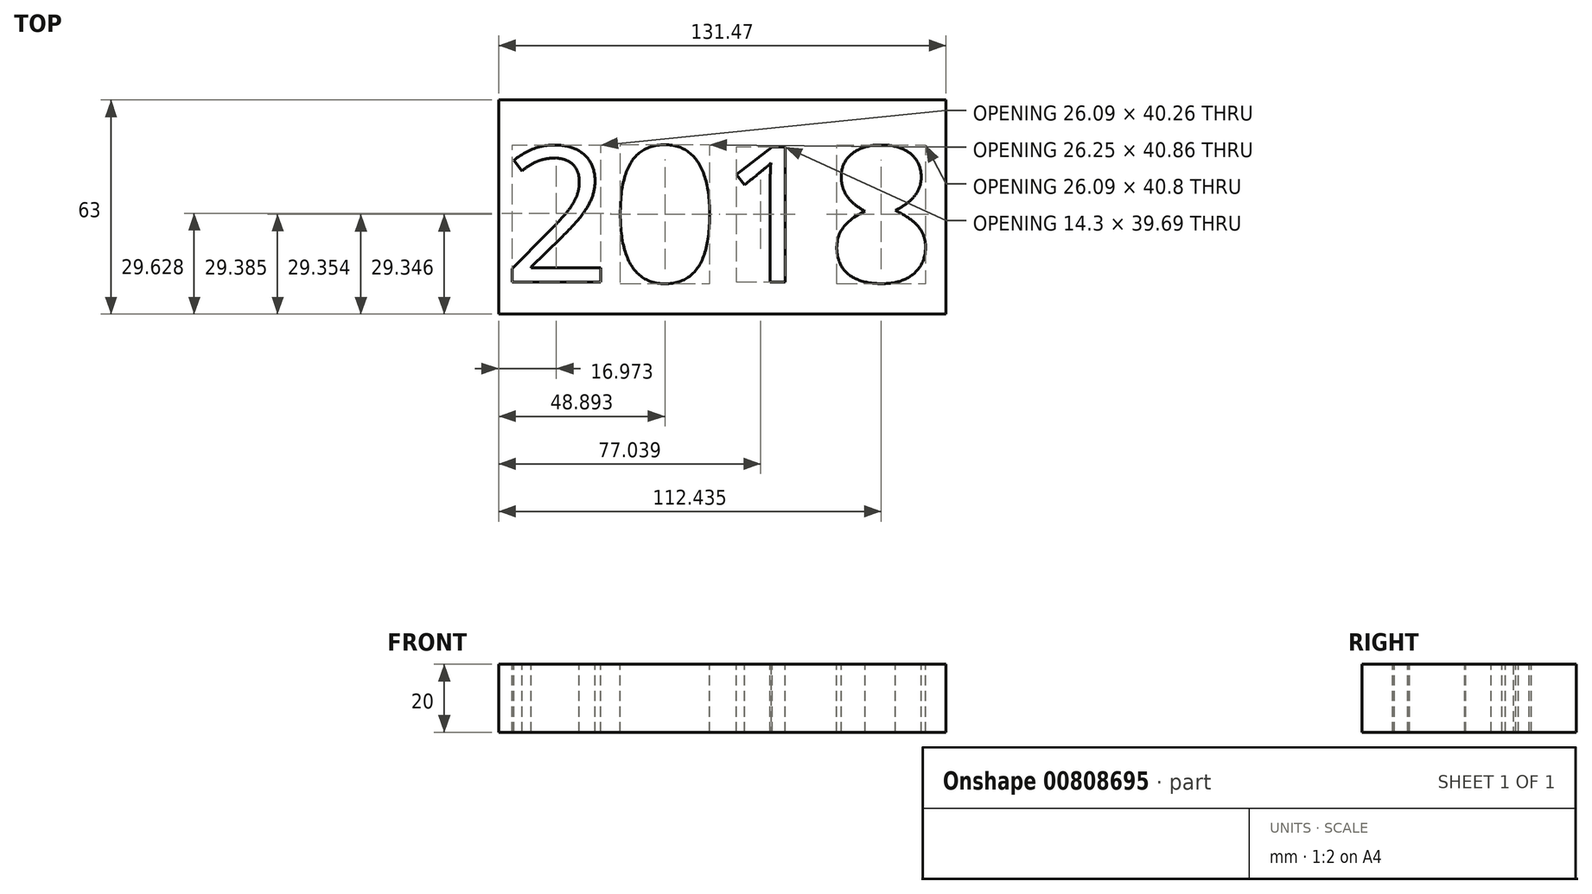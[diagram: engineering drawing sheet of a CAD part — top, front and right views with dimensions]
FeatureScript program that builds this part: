
annotation { "Feature Type Name" : "Feature", "Feature Type Description" : "" }
export const myFeature = defineFeature(function(context is Context, id is Id, definition is map)
    precondition{}
    {
        {
            var Q0;
            Q0=qCreatedBy(makeId("Top.planeOp"),FACE);
            var sketch = newSketch(context, id + "F0", { "sketchPlane" : qUnion([Q0])});
            skLineSegment(sketch, "E0.bottom", {"start": v(-131.47, 0) * mm, "end": v(0, 0) * mm});
            skLineSegment(sketch, "E0.top", {"start": v(-131.47, -63) * mm, "end": v(0, -63) * mm});
            skLineSegment(sketch, "E0.left", {"start": v(-131.47, 0) * mm, "end": v(-131.47, -63) * mm});
            skLineSegment(sketch, "E0.right", {"start": v(0, 0) * mm, "end": v(0, -63) * mm});
            skText(sketch, "E1", { "text": "2018\n", "fontName": "OpenSans-Regular.ttf"});
            const initialGuessF0  = {"E1": [-0.13026, -0.0535, 1, 0, 0.04003]};
            skSetInitialGuess(sketch, initialGuessF0);
            skSolve(sketch);
        }
        {
            var Q0;
            Q0=makeQuery(id+"F0.imprint","IMPRINT",FACE,{"disambiguationData":[TD([[makeQuery(id+"F0.imprint","IMPRINT",EDGE,{"derivedFrom":sQuery(id+"F0.wireOp",EDGE,"E0.bottom")}),-1.0]])]});
            extrude(context, id + "F1", {"entities" : qUnion([Q0]), "oppositeDirection" : true, "depth" : 20 * mm, "offsetDistance" : 25 * mm});
        }
    });
